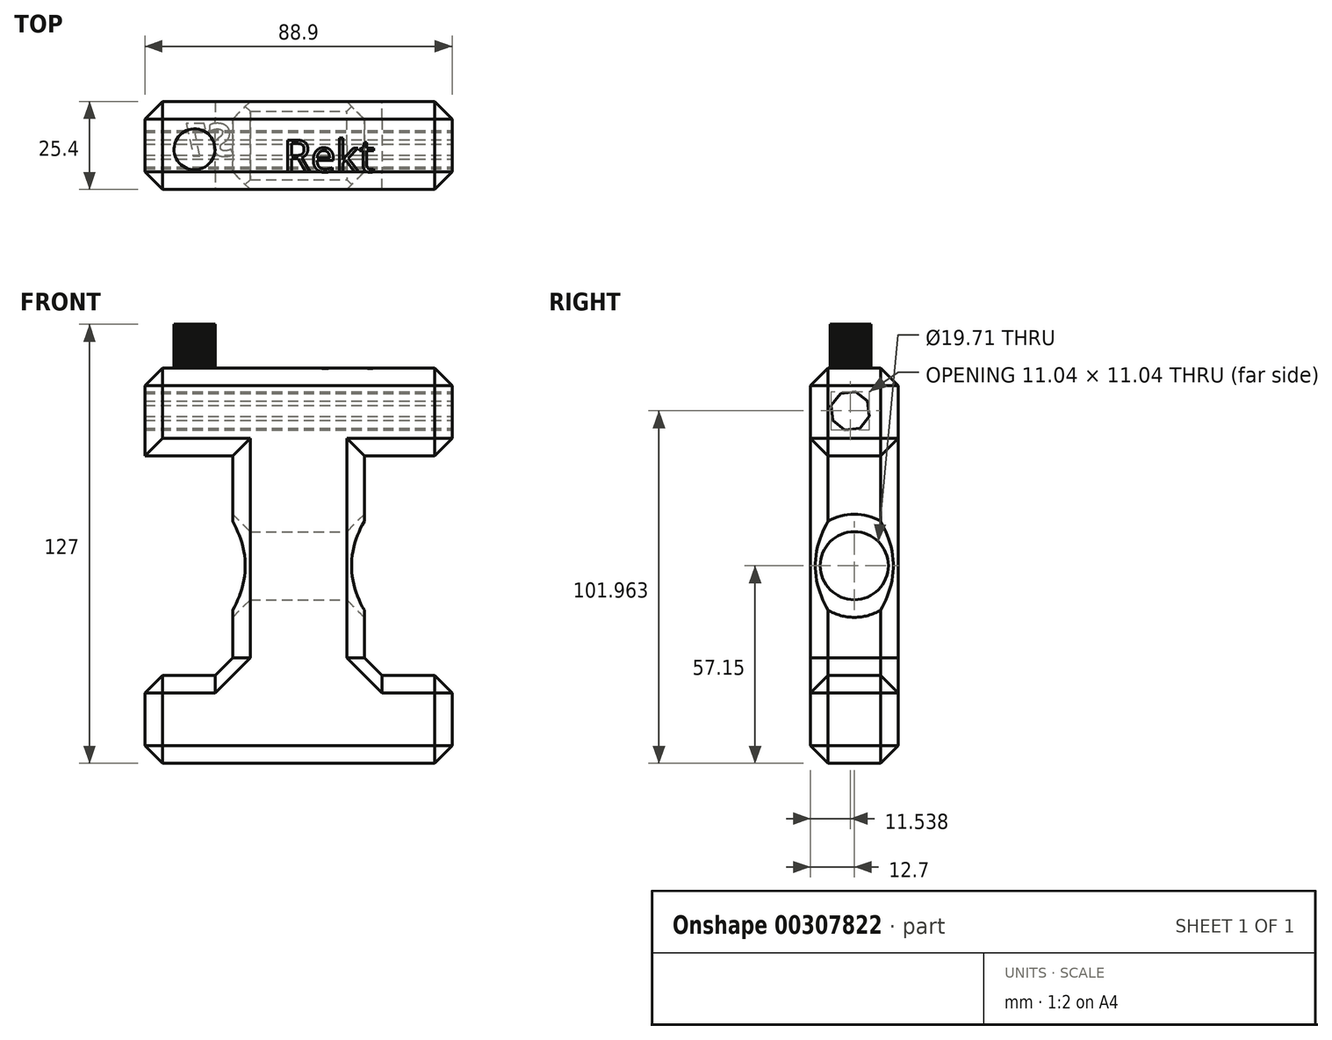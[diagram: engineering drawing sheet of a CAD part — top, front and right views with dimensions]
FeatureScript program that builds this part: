
annotation { "Feature Type Name" : "Feature", "Feature Type Description" : "" }
export const myFeature = defineFeature(function(context is Context, id is Id, definition is map)
    precondition{}
    {
        {
            var Q0;
            Q0=qCreatedBy(makeId("Front.planeOp"),FACE);
            var sketch = newSketch(context, id + "F0", { "sketchPlane" : qUnion([Q0])});
            skLineSegment(sketch, "E0", {"start": v(-41.8, -25.4) * mm, "end": v(47.1, -25.4) * mm});
            skLineSegment(sketch, "E1", {"start": v(47.1, -25.4) * mm, "end": v(47.1, 0) * mm});
            skLineSegment(sketch, "E2", {"start": v(47.1, 0) * mm, "end": v(21.7, 0) * mm});
            skLineSegment(sketch, "E3", {"start": v(21.7, 0) * mm, "end": v(21.7, 63.5) * mm});
            skLineSegment(sketch, "E4", {"start": v(21.7, 63.5) * mm, "end": v(47.1, 63.5) * mm});
            skLineSegment(sketch, "E5", {"start": v(47.1, 63.5) * mm, "end": v(47.1, 88.9) * mm});
            skLineSegment(sketch, "E6", {"start": v(47.1, 88.9) * mm, "end": v(-41.8, 88.9) * mm});
            skLineSegment(sketch, "E7", {"start": v(-41.8, 88.9) * mm, "end": v(-41.8, 63.5) * mm});
            skLineSegment(sketch, "E8", {"start": v(-41.8, 63.5) * mm, "end": v(-16.4, 63.5) * mm});
            skLineSegment(sketch, "E9", {"start": v(-16.4, 63.5) * mm, "end": v(-16.4, 0) * mm});
            skLineSegment(sketch, "E10", {"start": v(-16.4, 0) * mm, "end": v(-41.8, 0) * mm});
            skLineSegment(sketch, "E11", {"start": v(-41.8, 0) * mm, "end": v(-41.8, -25.4) * mm});
            skSolve(sketch);
        }
        {
            var Q0;
            Q0=makeQuery(id+"F0.imprint","IMPRINT",FACE,{"disambiguationData":[TD([[makeQuery(id+"F0.imprint","IMPRINT",EDGE,{"derivedFrom":sQuery(id+"F0.wireOp",EDGE,"E0")}),1.0]])]});
            extrude(context, id + "F1", {"entities" : qUnion([Q0]), "depth" : 25.4 * mm});
        }
        {
            var Q0;
            Q0=makeQuery(id+"F1.opExtrude","SWEPT_FACE",FACE,{"disambiguationData":[OSD([sQuery(id+"F0.wireOp",EDGE,"E3")])]});
            var sketch = newSketch(context, id + "F2", { "sketchPlane" : qUnion([Q0])});
            skCircle(sketch, "E12", {"center": v(-12.7, 31.75) * mm, "radius": 9.86 * mm});
            skPoint(sketch, "E12.centerSnap0", {"position": v(0, 31.75) * mm});
            skPoint(sketch, "E12.centerSnap1", {"position": v(-12.7, 0) * mm});
            skSolve(sketch);
        }
        {
            var Q0;
            Q0=makeQuery(id+"F2.imprint","IMPRINT",FACE,{"disambiguationData":[TD([[makeQuery(id+"F2.imprint","IMPRINT",EDGE,{"derivedFrom":sQuery(id+"F2.wireOp",EDGE,"E12")}),1.0]])]});
            extrude(context, id + "F3", {"entities" : qUnion([Q0]), "operationType" : NewBodyOperationType.REMOVE, "endBound" : BoundingType.THROUGH_ALL, "oppositeDirection" : true, "depth" : 25.4 * mm});
        }
        {
            var Q0;
            Q0=makeQuery(id+"F1.opExtrude","CAP_FACE",FACE,{"disambiguationData":[OSD([sQuery(id+"F0.wireOp",EDGE,"E0"),sQuery(id+"F0.wireOp",EDGE,"E1"),sQuery(id+"F0.wireOp",EDGE,"E2"),sQuery(id+"F0.wireOp",EDGE,"E3"),sQuery(id+"F0.wireOp",EDGE,"E4"),sQuery(id+"F0.wireOp",EDGE,"E5"),sQuery(id+"F0.wireOp",EDGE,"E6"),sQuery(id+"F0.wireOp",EDGE,"E7"),sQuery(id+"F0.wireOp",EDGE,"E8"),sQuery(id+"F0.wireOp",EDGE,"E9"),sQuery(id+"F0.wireOp",EDGE,"E10"),sQuery(id+"F0.wireOp",EDGE,"E11")])],"isStart":false});
            var Q1;
            Q1=makeQuery(id+"F1.opExtrude","SWEPT_FACE",FACE,{"disambiguationData":[OSD([sQuery(id+"F0.wireOp",EDGE,"E1")])]});
            var Q2;
            Q2=makeQuery(id+"F1.opExtrude","SWEPT_FACE",FACE,{"disambiguationData":[OSD([sQuery(id+"F0.wireOp",EDGE,"E2")])]});
            var Q3;
            Q3=makeQuery(id+"F1.opExtrude","SWEPT_FACE",FACE,{"disambiguationData":[OSD([sQuery(id+"F0.wireOp",EDGE,"E10")])]});
            var Q4;
            Q4=makeQuery(id+"F1.opExtrude","SWEPT_FACE",FACE,{"disambiguationData":[OSD([sQuery(id+"F0.wireOp",EDGE,"E6")])]});
            var Q5;
            Q5=makeQuery(id+"F1.opExtrude","SWEPT_FACE",FACE,{"disambiguationData":[OSD([sQuery(id+"F0.wireOp",EDGE,"E5")])]});
            var Q6;
            Q6=makeQuery(id+"F1.opExtrude","CAP_FACE",FACE,{"disambiguationData":[OSD([sQuery(id+"F0.wireOp",EDGE,"E0"),sQuery(id+"F0.wireOp",EDGE,"E1"),sQuery(id+"F0.wireOp",EDGE,"E2"),sQuery(id+"F0.wireOp",EDGE,"E3"),sQuery(id+"F0.wireOp",EDGE,"E4"),sQuery(id+"F0.wireOp",EDGE,"E5"),sQuery(id+"F0.wireOp",EDGE,"E6"),sQuery(id+"F0.wireOp",EDGE,"E7"),sQuery(id+"F0.wireOp",EDGE,"E8"),sQuery(id+"F0.wireOp",EDGE,"E9"),sQuery(id+"F0.wireOp",EDGE,"E10"),sQuery(id+"F0.wireOp",EDGE,"E11")])],"isStart":true});
            var Q7;
            Q7=makeQuery(id+"F1.opExtrude","SWEPT_FACE",FACE,{"disambiguationData":[OSD([sQuery(id+"F0.wireOp",EDGE,"E0")])]});
            var Q8;
            Q8=makeQuery(id+"F3.boolean.opBoolean","COPY",FACE,{"derivedFrom":makeQuery(id+"F3.opExtrude","SWEPT_FACE",FACE,{"disambiguationData":[OSD([sQuery(id+"F2.wireOp",EDGE,"E12")])]})});
            chamfer(context, id + "F4", {"entities" : qUnion([Q0, Q1, Q2, Q3, Q4, Q5, Q6, Q7, Q8]), "width" : 5.08 * mm, "tangentPropagation" : true});
        }
        {
            var Q0;
            Q0=makeQuery(id+"F1.opExtrude","SWEPT_FACE",FACE,{"disambiguationData":[OSD([sQuery(id+"F0.wireOp",EDGE,"E6")])]});
            var sketch = newSketch(context, id + "F5", { "sketchPlane" : qUnion([Q0])});
            skCircle(sketch, "E13.cCircle", {"center": v(-27.41, -13.8) * mm, "radius": 5.93 * mm, "construction": true});
            skLineSegment(sketch, "E13.0", {"start": v(-24.36, -18.87) * mm, "end": v(-25.02, -19.22) * mm});
            skLineSegment(sketch, "E13.1", {"start": v(-25.02, -19.22) * mm, "end": v(-25.72, -19.47) * mm});
            skLineSegment(sketch, "E13.2", {"start": v(-25.72, -19.47) * mm, "end": v(-26.45, -19.64) * mm});
            skLineSegment(sketch, "E13.3", {"start": v(-26.45, -19.64) * mm, "end": v(-27.19, -19.72) * mm});
            skLineSegment(sketch, "E13.4", {"start": v(-27.19, -19.72) * mm, "end": v(-27.93, -19.7) * mm});
            skLineSegment(sketch, "E13.5", {"start": v(-27.93, -19.7) * mm, "end": v(-28.67, -19.58) * mm});
            skLineSegment(sketch, "E13.6", {"start": v(-28.67, -19.58) * mm, "end": v(-29.38, -19.38) * mm});
            skLineSegment(sketch, "E13.7", {"start": v(-29.38, -19.38) * mm, "end": v(-30.07, -19.1) * mm});
            skLineSegment(sketch, "E13.8", {"start": v(-30.07, -19.1) * mm, "end": v(-30.71, -18.72) * mm});
            skLineSegment(sketch, "E13.9", {"start": v(-30.71, -18.72) * mm, "end": v(-31.3, -18.26) * mm});
            skLineSegment(sketch, "E13.10", {"start": v(-31.3, -18.26) * mm, "end": v(-31.83, -17.74) * mm});
            skLineSegment(sketch, "E13.11", {"start": v(-31.83, -17.74) * mm, "end": v(-32.3, -17.15) * mm});
            skLineSegment(sketch, "E13.12", {"start": v(-32.3, -17.15) * mm, "end": v(-32.68, -16.52) * mm});
            skLineSegment(sketch, "E13.13", {"start": v(-32.68, -16.52) * mm, "end": v(-32.98, -15.83) * mm});
            skLineSegment(sketch, "E13.14", {"start": v(-32.98, -15.83) * mm, "end": v(-33.19, -15.12) * mm});
            skLineSegment(sketch, "E13.15", {"start": v(-33.19, -15.12) * mm, "end": v(-33.3, -14.39) * mm});
            skLineSegment(sketch, "E13.16", {"start": v(-33.3, -14.39) * mm, "end": v(-33.34, -13.64) * mm});
            skLineSegment(sketch, "E13.17", {"start": v(-33.34, -13.64) * mm, "end": v(-33.27, -12.9) * mm});
            skLineSegment(sketch, "E13.18", {"start": v(-33.27, -12.9) * mm, "end": v(-33.11, -12.17) * mm});
            skLineSegment(sketch, "E13.19", {"start": v(-33.11, -12.17) * mm, "end": v(-32.87, -11.47) * mm});
            skLineSegment(sketch, "E13.20", {"start": v(-32.87, -11.47) * mm, "end": v(-32.53, -10.8) * mm});
            skLineSegment(sketch, "E13.21", {"start": v(-32.53, -10.8) * mm, "end": v(-32.12, -10.19) * mm});
            skLineSegment(sketch, "E13.22", {"start": v(-32.12, -10.19) * mm, "end": v(-31.63, -9.63) * mm});
            skLineSegment(sketch, "E13.23", {"start": v(-31.63, -9.63) * mm, "end": v(-31.07, -9.13) * mm});
            skLineSegment(sketch, "E13.24", {"start": v(-31.07, -9.13) * mm, "end": v(-30.46, -8.7) * mm});
            skLineSegment(sketch, "E13.25", {"start": v(-30.46, -8.7) * mm, "end": v(-29.8, -8.37) * mm});
            skLineSegment(sketch, "E13.26", {"start": v(-29.8, -8.37) * mm, "end": v(-29.1, -8.1) * mm});
            skLineSegment(sketch, "E13.27", {"start": v(-29.1, -8.1) * mm, "end": v(-28.37, -7.94) * mm});
            skLineSegment(sketch, "E13.28", {"start": v(-28.37, -7.94) * mm, "end": v(-27.63, -7.87) * mm});
            skLineSegment(sketch, "E13.29", {"start": v(-27.63, -7.87) * mm, "end": v(-26.9, -7.89) * mm});
            skLineSegment(sketch, "E13.30", {"start": v(-26.9, -7.89) * mm, "end": v(-26.15, -8) * mm});
            skLineSegment(sketch, "E13.31", {"start": v(-26.15, -8) * mm, "end": v(-25.44, -8.2) * mm});
            skLineSegment(sketch, "E13.32", {"start": v(-25.44, -8.2) * mm, "end": v(-24.75, -8.5) * mm});
            skLineSegment(sketch, "E13.33", {"start": v(-24.75, -8.5) * mm, "end": v(-24.1, -8.87) * mm});
            skLineSegment(sketch, "E13.34", {"start": v(-24.1, -8.87) * mm, "end": v(-23.52, -9.32) * mm});
            skLineSegment(sketch, "E13.35", {"start": v(-23.52, -9.32) * mm, "end": v(-22.99, -9.84) * mm});
            skLineSegment(sketch, "E13.36", {"start": v(-22.99, -9.84) * mm, "end": v(-22.53, -10.43) * mm});
            skLineSegment(sketch, "E13.37", {"start": v(-22.53, -10.43) * mm, "end": v(-22.15, -11.07) * mm});
            skLineSegment(sketch, "E13.38", {"start": v(-22.15, -11.07) * mm, "end": v(-21.85, -11.75) * mm});
            skLineSegment(sketch, "E13.39", {"start": v(-21.85, -11.75) * mm, "end": v(-21.63, -12.46) * mm});
            skLineSegment(sketch, "E13.40", {"start": v(-21.63, -12.46) * mm, "end": v(-21.51, -13.2) * mm});
            skLineSegment(sketch, "E13.41", {"start": v(-21.51, -13.2) * mm, "end": v(-21.48, -13.94) * mm});
            skLineSegment(sketch, "E13.42", {"start": v(-21.48, -13.94) * mm, "end": v(-21.55, -14.68) * mm});
            skLineSegment(sketch, "E13.43", {"start": v(-21.55, -14.68) * mm, "end": v(-21.7, -15.4) * mm});
            skLineSegment(sketch, "E13.44", {"start": v(-21.7, -15.4) * mm, "end": v(-21.96, -16.11) * mm});
            skLineSegment(sketch, "E13.45", {"start": v(-21.96, -16.11) * mm, "end": v(-22.29, -16.78) * mm});
            skLineSegment(sketch, "E13.46", {"start": v(-22.29, -16.78) * mm, "end": v(-22.7, -17.4) * mm});
            skLineSegment(sketch, "E13.47", {"start": v(-22.7, -17.4) * mm, "end": v(-23.2, -17.96) * mm});
            skLineSegment(sketch, "E13.48", {"start": v(-23.2, -17.96) * mm, "end": v(-23.75, -18.45) * mm});
            skLineSegment(sketch, "E13.49", {"start": v(-23.75, -18.45) * mm, "end": v(-24.36, -18.87) * mm});
            skText(sketch, "E14", { "text": "Rekt", "fontName": "OpenSans-Regular.ttf"});
            const initialGuessF5  = {"E14": [-0.0017, -0.02032, 1, 0, 0.00925]};
            skSetInitialGuess(sketch, initialGuessF5);
            skSolve(sketch);
        }
        {
            var Q0;
            Q0=makeQuery(id+"F5.imprint","IMPRINT",FACE,{"disambiguationData":[TD([[makeQuery(id+"F5.imprint","IMPRINT",EDGE,{"derivedFrom":sQuery(id+"F5.wireOp",EDGE,"E13.0")}),-1.0]])]});
            extrude(context, id + "F6", {"entities" : qUnion([Q0]), "operationType" : NewBodyOperationType.ADD, "depth" : 12.7 * mm});
        }
        {
            var Q0;
            Q0 = qSketchRegion(id + "F5", true);
            extrude(context, id + "F7", {"entities" : qUnion([Q0]), "operationType" : NewBodyOperationType.REMOVE, "oppositeDirection" : true, "depth" : 0.13 * mm});
        }
        {
            var Q0;
            Q0=makeQuery(id+"F1.opExtrude","SWEPT_FACE",FACE,{"disambiguationData":[OSD([sQuery(id+"F0.wireOp",EDGE,"E5")])]});
            var sketch = newSketch(context, id + "F8", { "sketchPlane" : qUnion([Q0])});
            skCircle(sketch, "E15.cCircle", {"center": v(-13.86, 76.56) * mm, "radius": 5.75 * mm, "construction": true});
            skLineSegment(sketch, "E15.0", {"start": v(-8.34, 74.97) * mm, "end": v(-11.09, 71.53) * mm});
            skLineSegment(sketch, "E15.1", {"start": v(-11.09, 71.53) * mm, "end": v(-15.46, 71.04) * mm});
            skLineSegment(sketch, "E15.2", {"start": v(-15.46, 71.04) * mm, "end": v(-18.9, 73.8) * mm});
            skLineSegment(sketch, "E15.3", {"start": v(-18.9, 73.8) * mm, "end": v(-19.38, 78.16) * mm});
            skLineSegment(sketch, "E15.4", {"start": v(-19.38, 78.16) * mm, "end": v(-16.63, 81.6) * mm});
            skLineSegment(sketch, "E15.5", {"start": v(-16.63, 81.6) * mm, "end": v(-12.26, 82.08) * mm});
            skLineSegment(sketch, "E15.6", {"start": v(-12.26, 82.08) * mm, "end": v(-8.83, 79.34) * mm});
            skLineSegment(sketch, "E15.7", {"start": v(-8.83, 79.34) * mm, "end": v(-8.34, 74.97) * mm});
            skSolve(sketch);
        }
        {
            var Q0;
            Q0=makeQuery(id+"F8.imprint","IMPRINT",FACE,{"disambiguationData":[TD([[makeQuery(id+"F8.imprint","IMPRINT",EDGE,{"derivedFrom":sQuery(id+"F8.wireOp",EDGE,"E15.0")}),-1.0]])]});
            extrude(context, id + "F9", {"entities" : qUnion([Q0]), "operationType" : NewBodyOperationType.REMOVE, "endBound" : BoundingType.THROUGH_ALL, "oppositeDirection" : true, "depth" : 25.4 * mm});
        }
        {
            var Q0;
            Q0=makeQuery(id+"F1.opExtrude","SWEPT_FACE",FACE,{"disambiguationData":[OSD([sQuery(id+"F0.wireOp",EDGE,"E0")])]});
            var sketch = newSketch(context, id + "F10", { "sketchPlane" : qUnion([Q0])});
            skText(sketch, "E16", { "text": "LS", "fontName": "OpenSans-BoldItalic.ttf"});
            const initialGuessF10  = {"E16": [-0.03013, 0.0064, 1, 0, 0.00946]};
            skSetInitialGuess(sketch, initialGuessF10);
            skSolve(sketch);
        }
        {
            var Q0;
            Q0 = qSketchRegion(id + "F10", true);
            extrude(context, id + "F11", {"entities" : qUnion([Q0]), "operationType" : NewBodyOperationType.REMOVE, "oppositeDirection" : true, "depth" : 0.13 * mm});
        }
    });
